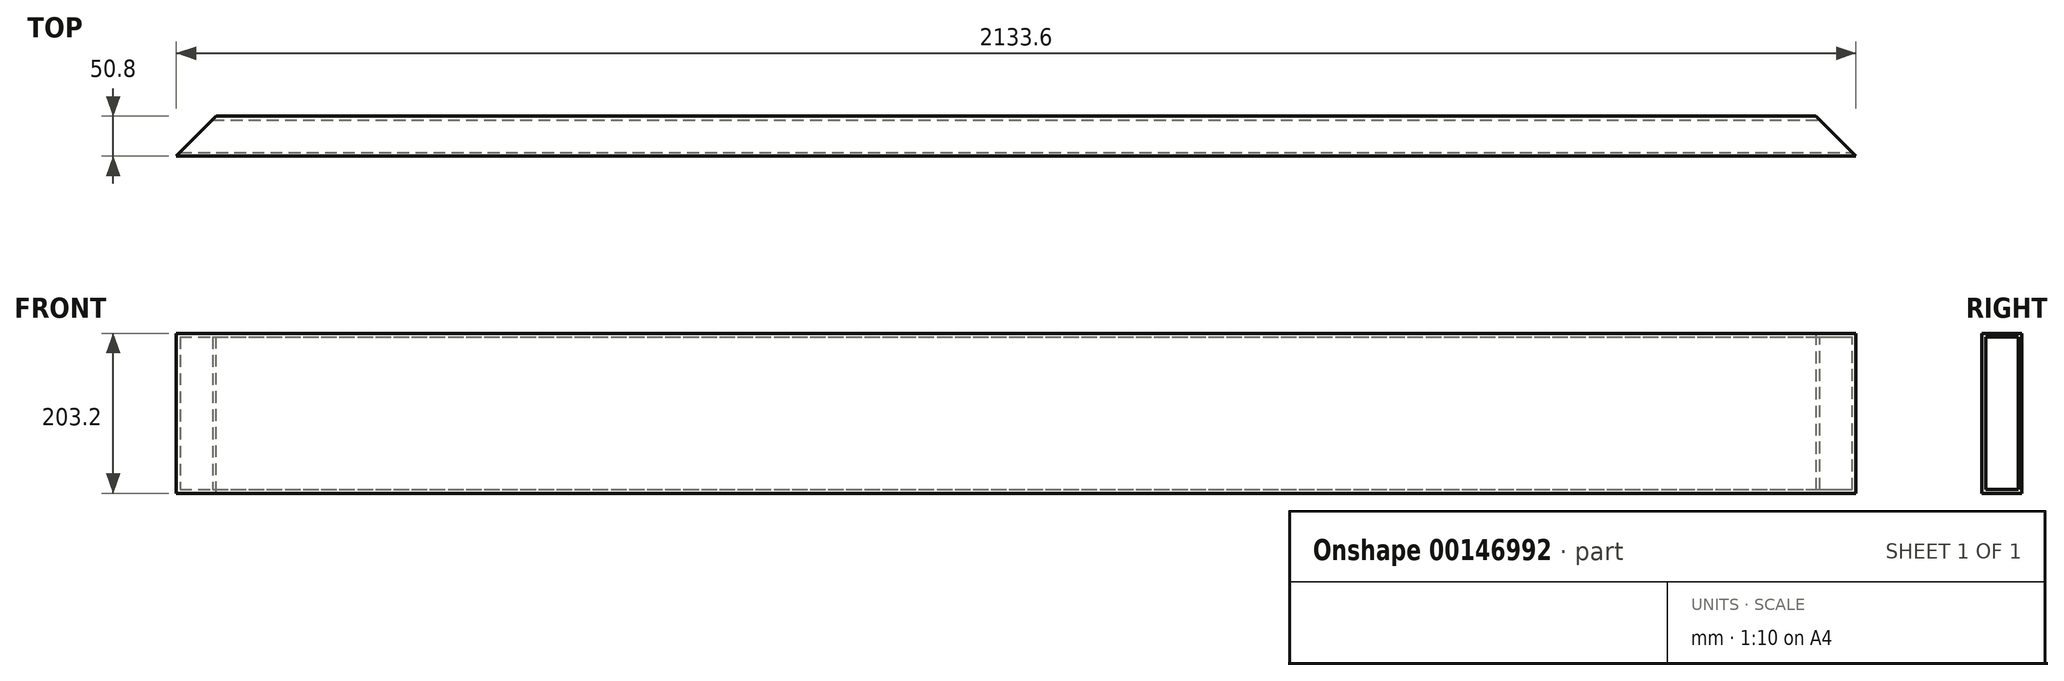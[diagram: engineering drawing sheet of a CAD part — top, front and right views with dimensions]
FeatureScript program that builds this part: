
annotation { "Feature Type Name" : "Feature", "Feature Type Description" : "" }
export const myFeature = defineFeature(function(context is Context, id is Id, definition is map)
    precondition{}
    {
        {
            var Q0;
            Q0=qCreatedBy(makeId("Right.planeOp"),FACE);
            var sketch = newSketch(context, id + "F0", { "sketchPlane" : qUnion([Q0])});
            skLineSegment(sketch, "E0.bottom", {"start": v(0, 0) * mm, "end": v(50.8, 0) * mm});
            skLineSegment(sketch, "E0.top", {"start": v(0, 203.2) * mm, "end": v(50.8, 203.2) * mm});
            skLineSegment(sketch, "E0.left", {"start": v(0, 0) * mm, "end": v(0, 203.2) * mm});
            skLineSegment(sketch, "E0.right", {"start": v(50.8, 0) * mm, "end": v(50.8, 203.2) * mm});
            skLineSegment(sketch, "E1.bottom", {"start": v(4.76, 198.44) * mm, "end": v(46.04, 198.44) * mm});
            skLineSegment(sketch, "E1.top", {"start": v(4.76, 4.76) * mm, "end": v(46.04, 4.76) * mm});
            skLineSegment(sketch, "E1.left", {"start": v(4.76, 198.44) * mm, "end": v(4.76, 4.76) * mm});
            skLineSegment(sketch, "E1.right", {"start": v(46.04, 198.44) * mm, "end": v(46.04, 4.76) * mm});
            skSolve(sketch);
        }
        {
            var Q0;
            Q0=makeQuery(id+"F0.imprint","IMPRINT",FACE,{"disambiguationData":[TD([[makeQuery(id+"F0.imprint","IMPRINT",EDGE,{"derivedFrom":sQuery(id+"F0.wireOp",EDGE,"E0.bottom")}),1.0]])]});
            extrude(context, id + "F1", {"entities" : qUnion([Q0]), "oppositeDirection" : true, "depth" : 2133.6 * mm});
        }
        {
            var Q0;
            Q0=makeQuery(id+"F1.opExtrude","CAP_EDGE",EDGE,{"disambiguationData":[OSD([sQuery(id+"F0.wireOp",EDGE,"E0.right")])],"isStart":true});
            chamfer(context, id + "F2", {"entities" : qUnion([Q0]), "width" : 50.8 * mm, "tangentPropagation" : true});
        }
        {
            var Q0;
            Q0=makeQuery(id+"F1.opExtrude","CAP_EDGE",EDGE,{"disambiguationData":[OSD([sQuery(id+"F0.wireOp",EDGE,"E0.right")])],"isStart":false});
            chamfer(context, id + "F3", {"entities" : qUnion([Q0]), "width" : 50.8 * mm, "tangentPropagation" : true});
        }
    });
